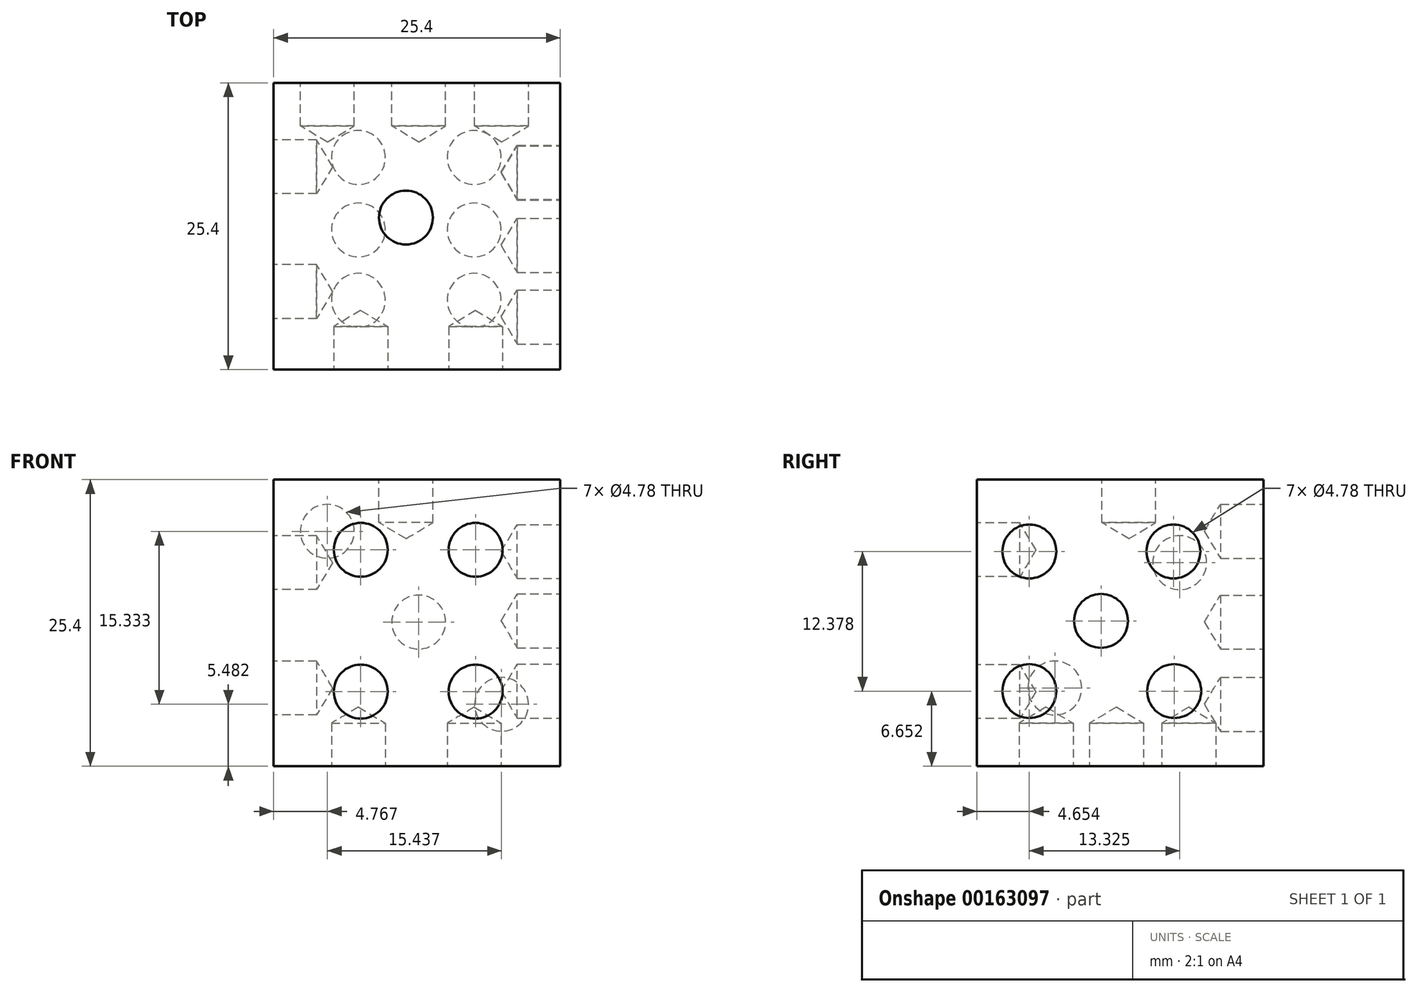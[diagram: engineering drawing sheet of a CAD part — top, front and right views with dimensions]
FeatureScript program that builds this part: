
annotation { "Feature Type Name" : "Feature", "Feature Type Description" : "" }
export const myFeature = defineFeature(function(context is Context, id is Id, definition is map)
    precondition{}
    {
        {
            var Q0;
            Q0=qCreatedBy(makeId("Top.planeOp"),FACE);
            var sketch = newSketch(context, id + "F0", { "sketchPlane" : qUnion([Q0])});
            skLineSegment(sketch, "E0.bottom", {"start": v(0, 0) * mm, "end": v(25.4, 0) * mm});
            skLineSegment(sketch, "E0.top", {"start": v(0, 25.4) * mm, "end": v(25.4, 25.4) * mm});
            skLineSegment(sketch, "E0.left", {"start": v(0, 0) * mm, "end": v(0, 25.4) * mm});
            skLineSegment(sketch, "E0.right", {"start": v(25.4, 0) * mm, "end": v(25.4, 25.4) * mm});
            skSolve(sketch);
        }
        {
            var Q0;
            Q0 = qSketchRegion(id + "F0", true);
            extrude(context, id + "F1", {"entities" : qUnion([Q0]), "depth" : 25.4 * mm});
        }
        {
            var Q0;
            Q0=makeQuery(id+"F1.opExtrude","CAP_FACE",FACE,{"disambiguationData":[OSD([sQuery(id+"F0.wireOp",EDGE,"E0.bottom"),sQuery(id+"F0.wireOp",EDGE,"E0.top"),sQuery(id+"F0.wireOp",EDGE,"E0.left"),sQuery(id+"F0.wireOp",EDGE,"E0.right")])],"isStart":false});
            var sketch = newSketch(context, id + "F2", { "sketchPlane" : qUnion([Q0])});
            skPoint(sketch, "E1", {"position": v(11.73, 13.47) * mm});
            skSolve(sketch);
        }
        {
            var Q0;
            Q0=sQuery(id+"F2.wireOp",VERTEX,"E1");
            var Q1;
            Q1=makeQuery(id+"F1.opExtrude","SWEPT_BODY",BODY,{"disambiguationData":[OSD([sQuery(id+"F0.wireOp",EDGE,"E0.bottom"),sQuery(id+"F0.wireOp",EDGE,"E0.top"),sQuery(id+"F0.wireOp",EDGE,"E0.left"),sQuery(id+"F0.wireOp",EDGE,"E0.right")])]});
            hole(context, id + "F3", {"style" : HoleStyle.SIMPLE, "endStyle" : HoleEndStyle.BLIND, "holeDiameter" : 4.78 * mm, "holeDepth" : 3.8 * mm, "locations" : qUnion([Q0]), "scope" : qUnion([Q1])});
        }
        {
            var Q0;
            Q0=makeQuery(id+"F1.opExtrude","CAP_FACE",FACE,{"disambiguationData":[OSD([sQuery(id+"F0.wireOp",EDGE,"E0.bottom"),sQuery(id+"F0.wireOp",EDGE,"E0.top"),sQuery(id+"F0.wireOp",EDGE,"E0.left"),sQuery(id+"F0.wireOp",EDGE,"E0.right")])],"isStart":true});
            cPlane(context, id + "F4", {"entities" : qUnion([Q0]), "cplaneType" : CPlaneType.OFFSET, "offset" : 0 * mm, "width" : 152.4 * mm, "height" : 152.4 * mm});
        }
        {
            var Q0;
            Q0=qCreatedBy(id+"F4.planeOp",FACE);
            var sketch = newSketch(context, id + "F5", { "sketchPlane" : qUnion([Q0])});
            skPoint(sketch, "E2", {"position": v(7.52, -6.14) * mm});
            skPoint(sketch, "E3", {"position": v(7.52, -12.37) * mm});
            skPoint(sketch, "E4", {"position": v(7.52, -18.79) * mm});
            skPoint(sketch, "E5", {"position": v(17.78, -18.79) * mm});
            skPoint(sketch, "E6", {"position": v(17.78, -12.37) * mm});
            skPoint(sketch, "E7", {"position": v(17.78, -6.14) * mm});
            skSolve(sketch);
        }
        {
            var Q0;
            Q0=sQuery(id+"F5.wireOp",VERTEX,"E2");
            var Q1;
            Q1=sQuery(id+"F5.wireOp",VERTEX,"E7");
            var Q2;
            Q2=sQuery(id+"F5.wireOp",VERTEX,"E3");
            var Q3;
            Q3=sQuery(id+"F5.wireOp",VERTEX,"E6");
            var Q4;
            Q4=sQuery(id+"F5.wireOp",VERTEX,"E5");
            var Q5;
            Q5=sQuery(id+"F5.wireOp",VERTEX,"E4");
            var Q6;
            Q6=makeQuery(id+"F1.opExtrude","SWEPT_BODY",BODY,{"disambiguationData":[OSD([sQuery(id+"F0.wireOp",EDGE,"E0.bottom"),sQuery(id+"F0.wireOp",EDGE,"E0.top"),sQuery(id+"F0.wireOp",EDGE,"E0.left"),sQuery(id+"F0.wireOp",EDGE,"E0.right")])]});
            hole(context, id + "F6", {"style" : HoleStyle.SIMPLE, "endStyle" : HoleEndStyle.BLIND, "holeDiameter" : 4.78 * mm, "holeDepth" : 3.8 * mm, "locations" : qUnion([Q0, Q1, Q2, Q3, Q4, Q5]), "scope" : qUnion([Q6])});
        }
        {
            var Q0;
            Q0=makeQuery(id+"F1.opExtrude","SWEPT_FACE",FACE,{"disambiguationData":[OSD([sQuery(id+"F0.wireOp",EDGE,"E0.right")])]});
            cPlane(context, id + "F7", {"entities" : qUnion([Q0]), "cplaneType" : CPlaneType.OFFSET, "offset" : 0 * mm, "width" : 152.4 * mm, "height" : 152.4 * mm});
        }
        {
            var Q0;
            Q0=qCreatedBy(id+"F7.planeOp",FACE);
            var sketch = newSketch(context, id + "F8", { "sketchPlane" : qUnion([Q0])});
            skPoint(sketch, "E8", {"position": v(17.49, 6.65) * mm});
            skPoint(sketch, "E9", {"position": v(17.42, 19.03) * mm});
            skPoint(sketch, "E10", {"position": v(4.65, 19.03) * mm});
            skPoint(sketch, "E11", {"position": v(4.65, 6.65) * mm});
            skPoint(sketch, "E12", {"position": v(11, 12.87) * mm});
            skSolve(sketch);
        }
        {
            var Q0;
            Q0=makeQuery(id+"F1.opExtrude","SWEPT_FACE",FACE,{"disambiguationData":[OSD([sQuery(id+"F0.wireOp",EDGE,"E0.left")])]});
            cPlane(context, id + "F9", {"entities" : qUnion([Q0]), "cplaneType" : CPlaneType.OFFSET, "offset" : 0 * mm, "width" : 152.4 * mm, "height" : 152.4 * mm});
        }
        {
            var Q0;
            Q0=qCreatedBy(id+"F9.planeOp",FACE);
            var sketch = newSketch(context, id + "F10", { "sketchPlane" : qUnion([Q0])});
            skPoint(sketch, "E13", {"position": v(-6.9, 6.93) * mm});
            skPoint(sketch, "E14", {"position": v(-17.98, 18.04) * mm});
            skSolve(sketch);
        }
        {
            var Q0;
            Q0=sQuery(id+"F10.wireOp",VERTEX,"E14");
            var Q1;
            Q1=sQuery(id+"F10.wireOp",VERTEX,"E13");
            var Q2;
            Q2=makeQuery(id+"F1.opExtrude","SWEPT_BODY",BODY,{"disambiguationData":[OSD([sQuery(id+"F0.wireOp",EDGE,"E0.bottom"),sQuery(id+"F0.wireOp",EDGE,"E0.top"),sQuery(id+"F0.wireOp",EDGE,"E0.left"),sQuery(id+"F0.wireOp",EDGE,"E0.right")])]});
            hole(context, id + "F11", {"style" : HoleStyle.SIMPLE, "endStyle" : HoleEndStyle.BLIND, "holeDiameter" : 4.78 * mm, "holeDepth" : 3.8 * mm, "locations" : qUnion([Q0, Q1]), "scope" : qUnion([Q2])});
        }
        {
            var Q0;
            Q0=makeQuery(id+"F1.opExtrude","SWEPT_FACE",FACE,{"disambiguationData":[OSD([sQuery(id+"F0.wireOp",EDGE,"E0.top")])]});
            cPlane(context, id + "F12", {"entities" : qUnion([Q0]), "cplaneType" : CPlaneType.OFFSET, "offset" : 0 * mm, "width" : 152.4 * mm, "height" : 152.4 * mm});
        }
        {
            var Q0;
            Q0=qCreatedBy(id+"F12.planeOp",FACE);
            var sketch = newSketch(context, id + "F13", { "sketchPlane" : qUnion([Q0])});
            skPoint(sketch, "E15", {"position": v(-12.86, 12.78) * mm});
            skPoint(sketch, "E16", {"position": v(-20.2, 5.48) * mm});
            skPoint(sketch, "E17", {"position": v(-4.77, 20.82) * mm});
            skSolve(sketch);
        }
        {
            var Q0;
            Q0=sQuery(id+"F13.wireOp",VERTEX,"E17");
            var Q1;
            Q1=sQuery(id+"F13.wireOp",VERTEX,"E15");
            var Q2;
            Q2=sQuery(id+"F13.wireOp",VERTEX,"E16");
            var Q3;
            Q3=makeQuery(id+"F1.opExtrude","SWEPT_BODY",BODY,{"disambiguationData":[OSD([sQuery(id+"F0.wireOp",EDGE,"E0.bottom"),sQuery(id+"F0.wireOp",EDGE,"E0.top"),sQuery(id+"F0.wireOp",EDGE,"E0.left"),sQuery(id+"F0.wireOp",EDGE,"E0.right")])]});
            hole(context, id + "F14", {"style" : HoleStyle.SIMPLE, "endStyle" : HoleEndStyle.BLIND, "holeDiameter" : 4.78 * mm, "holeDepth" : 3.8 * mm, "locations" : qUnion([Q0, Q1, Q2]), "scope" : qUnion([Q3])});
        }
        {
            var Q0;
            Q0=sQuery(id+"F8.wireOp",VERTEX,"E10");
            var Q1;
            Q1=sQuery(id+"F8.wireOp",VERTEX,"E11");
            var Q2;
            Q2=sQuery(id+"F8.wireOp",VERTEX,"E12");
            var Q3;
            Q3=sQuery(id+"F8.wireOp",VERTEX,"E9");
            var Q4;
            Q4=sQuery(id+"F8.wireOp",VERTEX,"E8");
            var Q5;
            Q5=makeQuery(id+"F1.opExtrude","SWEPT_BODY",BODY,{"disambiguationData":[OSD([sQuery(id+"F0.wireOp",EDGE,"E0.bottom"),sQuery(id+"F0.wireOp",EDGE,"E0.top"),sQuery(id+"F0.wireOp",EDGE,"E0.left"),sQuery(id+"F0.wireOp",EDGE,"E0.right")])]});
            hole(context, id + "F15", {"style" : HoleStyle.SIMPLE, "endStyle" : HoleEndStyle.BLIND, "holeDiameter" : 4.78 * mm, "holeDepth" : 3.8 * mm, "locations" : qUnion([Q0, Q1, Q2, Q3, Q4]), "scope" : qUnion([Q5])});
        }
        {
            var Q0;
            Q0=makeQuery(id+"F1.opExtrude","SWEPT_FACE",FACE,{"disambiguationData":[OSD([sQuery(id+"F0.wireOp",EDGE,"E0.bottom")])]});
            cPlane(context, id + "F16", {"entities" : qUnion([Q0]), "cplaneType" : CPlaneType.OFFSET, "offset" : 0 * mm, "width" : 152.4 * mm, "height" : 152.4 * mm});
        }
        {
            var Q0;
            Q0=qCreatedBy(id+"F16.planeOp",FACE);
            var sketch = newSketch(context, id + "F17", { "sketchPlane" : qUnion([Q0])});
            skPoint(sketch, "E18", {"position": v(7.73, 19.18) * mm});
            skPoint(sketch, "E19", {"position": v(17.9, 19.18) * mm});
            skPoint(sketch, "E20", {"position": v(17.9, 6.61) * mm});
            skPoint(sketch, "E21", {"position": v(7.73, 6.61) * mm});
            skSolve(sketch);
        }
        {
            var Q0;
            Q0=sQuery(id+"F17.wireOp",VERTEX,"E18");
            var Q1;
            Q1=sQuery(id+"F17.wireOp",VERTEX,"E19");
            var Q2;
            Q2=sQuery(id+"F17.wireOp",VERTEX,"E20");
            var Q3;
            Q3=sQuery(id+"F17.wireOp",VERTEX,"E21");
            var Q4;
            Q4=makeQuery(id+"F1.opExtrude","SWEPT_BODY",BODY,{"disambiguationData":[OSD([sQuery(id+"F0.wireOp",EDGE,"E0.bottom"),sQuery(id+"F0.wireOp",EDGE,"E0.top"),sQuery(id+"F0.wireOp",EDGE,"E0.left"),sQuery(id+"F0.wireOp",EDGE,"E0.right")])]});
            hole(context, id + "F18", {"style" : HoleStyle.SIMPLE, "endStyle" : HoleEndStyle.BLIND, "holeDiameter" : 4.78 * mm, "holeDepth" : 3.8 * mm, "locations" : qUnion([Q0, Q1, Q2, Q3]), "scope" : qUnion([Q4])});
        }
    });
